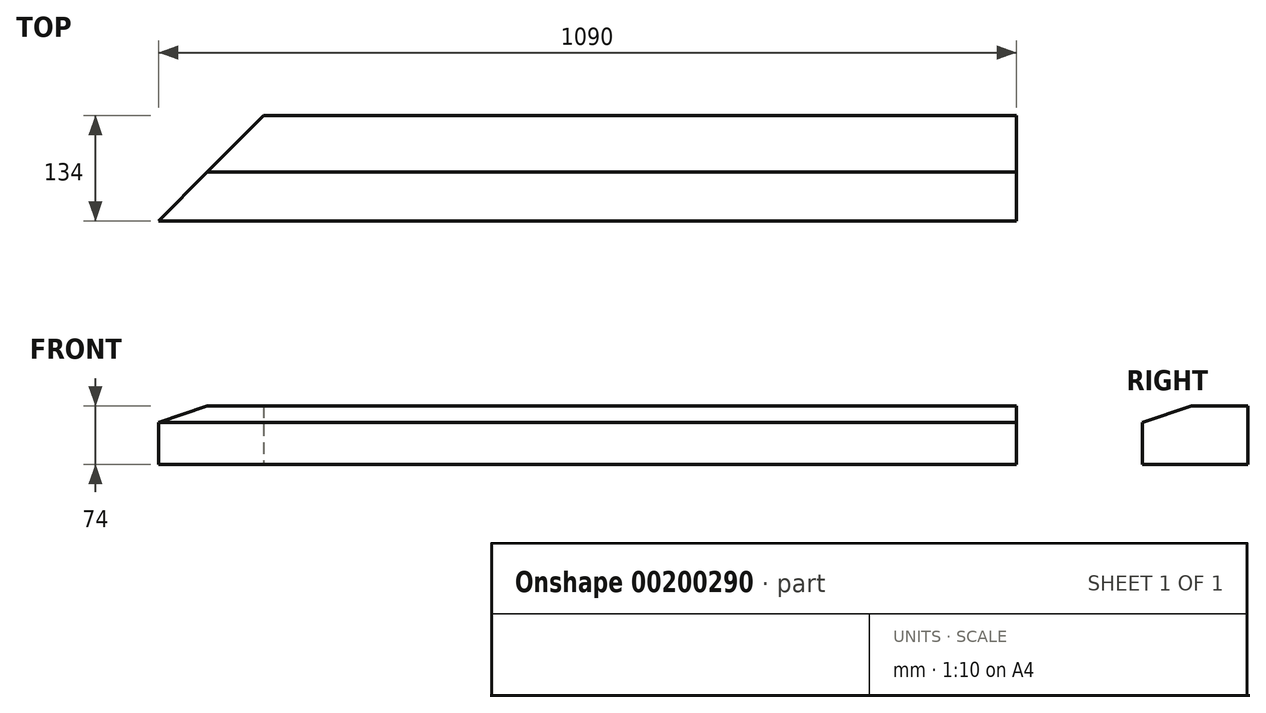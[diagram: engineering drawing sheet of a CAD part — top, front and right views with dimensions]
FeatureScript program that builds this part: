
annotation { "Feature Type Name" : "Feature", "Feature Type Description" : "" }
export const myFeature = defineFeature(function(context is Context, id is Id, definition is map)
    precondition{}
    {
        {
            var Q0;
            Q0=qCreatedBy(makeId("Right.planeOp"),FACE);
            var sketch = newSketch(context, id + "F0", { "sketchPlane" : qUnion([Q0])});
            skLineSegment(sketch, "E0", {"start": v(0, 0) * mm, "end": v(0, 74) * mm});
            skLineSegment(sketch, "E1", {"start": v(0, 74) * mm, "end": v(-72, 74) * mm});
            skLineSegment(sketch, "E2", {"start": v(-72, 74) * mm, "end": v(-134, 53) * mm});
            skLineSegment(sketch, "E3", {"start": v(-134, 53) * mm, "end": v(-134, 0) * mm});
            skLineSegment(sketch, "E4", {"start": v(-134, 0) * mm, "end": v(0, 0) * mm});
            skSolve(sketch);
        }
        {
            var Q0;
            Q0=makeQuery(id+"F0.imprint","IMPRINT",FACE,{"disambiguationData":[TD([[makeQuery(id+"F0.imprint","IMPRINT",EDGE,{"derivedFrom":sQuery(id+"F0.wireOp",EDGE,"E0")}),1.0]])]});
            extrude(context, id + "F1", {"entities" : qUnion([Q0]), "oppositeDirection" : true, "depth" : 1090 * mm, "offsetDistance" : 25 * mm});
        }
        {
            var Q0;
            Q0=qCreatedBy(makeId("Top.planeOp"),FACE);
            var sketch = newSketch(context, id + "F2", { "sketchPlane" : qUnion([Q0])});
            skLineSegment(sketch, "E5", {"start": v(-1090, -134) * mm, "end": v(-956.39, 0) * mm});
            skLineSegment(sketch, "E6", {"start": v(-956.39, 0) * mm, "end": v(-1195.4, 0) * mm});
            skLineSegment(sketch, "E7", {"start": v(-1195.4, 0) * mm, "end": v(-1195.4, -137.2) * mm});
            skLineSegment(sketch, "E8", {"start": v(-1195.4, -137.2) * mm, "end": v(-1090, -134) * mm});
            skSolve(sketch);
        }
        {
            var Q0;
            Q0=makeQuery(id+"F2.imprint","IMPRINT",FACE,{"disambiguationData":[TD([[makeQuery(id+"F2.imprint","IMPRINT",EDGE,{"derivedFrom":sQuery(id+"F2.wireOp",EDGE,"E5")}),1.0]])]});
            extrude(context, id + "F3", {"entities" : qUnion([Q0]), "operationType" : NewBodyOperationType.REMOVE, "endBound" : BoundingType.THROUGH_ALL, "depth" : 25 * mm, "offsetDistance" : 25 * mm});
        }
    });
